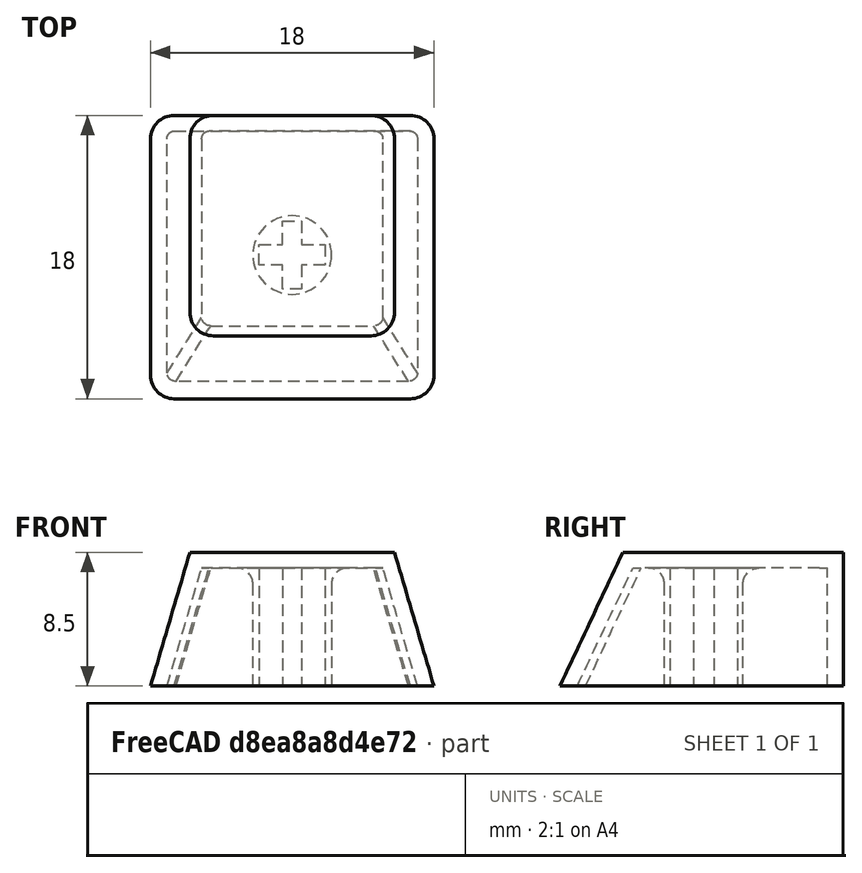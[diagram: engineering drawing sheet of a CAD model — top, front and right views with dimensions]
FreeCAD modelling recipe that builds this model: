
FCSTD DOCUMENT  (FreeCAD 0.20R29603 (Git))
Label: basecapv2
License: All rights reserved
LicenseURL: http://en.wikipedia.org/wiki/All_rights_reserved
objects: Sketcher::SketchObject×3, PartDesign::AdditiveLoft×1, PartDesign::Thickness×1, Mesh::Feature×1, PartDesign::Pad×1, PartDesign::Fillet×1, PartDesign::Body×1
note: 12 computed .brp shape members not serialized (recipe doc carries the construction recipe); baked Part::Feature solids carry a one-line shape summary decoded from their .brp

FEATURE [Sketcher::SketchObject] Sketch
  AttachmentOffset = pos=(0,0,8.5) rot=(0,0,1;0rad)
  FullyConstrained = true
  MapMode = 5
  Placement = pos=(0,0,8.5) rot=(0,0,1;0rad)
  Support = -> [XY_Plane]
  sketch-geometry (8):
    g0: LineSegment StartX=1.5 StartY=0 StartZ=0 EndX=11.5 EndY=0 EndZ=0
    g1: LineSegment StartX=13 StartY=1.5 StartZ=0 EndX=13 EndY=12.5 EndZ=0
    g2: LineSegment StartX=11.5 StartY=14 StartZ=0 EndX=1.5 EndY=14 EndZ=0
    g3: LineSegment StartX=2.849e-13 StartY=12.5 StartZ=0 EndX=2.849e-13 EndY=1.5 EndZ=0
    g4: ArcOfCircle CenterX=1.5 CenterY=12.5 CenterZ=0 NormalX=0 NormalY=0 NormalZ=1 AngleXU=0 Radius=1.5 StartAngle=1.5708 EndAngle=3.14159
    g5: ArcOfCircle CenterX=11.5 CenterY=12.5 CenterZ=0 NormalX=0 NormalY=0 NormalZ=1 AngleXU=0 Radius=1.5 StartAngle=-9e-16 EndAngle=1.5708
    g6: ArcOfCircle CenterX=11.5 CenterY=1.5 CenterZ=0 NormalX=0 NormalY=0 NormalZ=1 AngleXU=0 Radius=1.5 StartAngle=4.71239 EndAngle=6.28319
    g7: ArcOfCircle CenterX=1.5 CenterY=1.5 CenterZ=0 NormalX=0 NormalY=0 NormalZ=1 AngleXU=0 Radius=1.5 StartAngle=3.14159 EndAngle=4.71239
  constraints (20):
    c: Horizontal(g0)
    c: Horizontal(g2)
    c: Vertical(g1)
    c: Vertical(g3)
    c: Tangent(g3,g4) = -1.5708
    c: Tangent(g2,g4) = -1.5708
    c: Tangent(g1,g5) = -1.5708
    c: Tangent(g2,g5) = -1.5708
    c: Tangent(g0,g6) = -1.5708
    c: Tangent(g1,g6) = -1.5708
    c: Tangent(g3,g7) = -1.5708
    c: Tangent(g0,g7) = -1.5708
    c: Equal(g7,g4)
    c: Equal(g4,g5)
    c: Equal(g5,g6)
    c: Diameter(g5) = 3
    c: DistanceX(g3,g1) = 13
    c: PointOnObject(g3,g-2)
    c: PointOnObject(g0,g-1)
    c: DistanceY(g0,g2) = 14
FEATURE [Sketcher::SketchObject] Sketch001
  ExternalGeometry = -> [Sketch]
  FullyConstrained = true
  MapMode = 5
  Support = -> [XY_Plane]
  sketch-geometry (12):
    g0: ArcOfCircle CenterX=-1 CenterY=12.5 CenterZ=0 NormalX=0 NormalY=0 NormalZ=1 AngleXU=0 Radius=1.5 StartAngle=1.5708 EndAngle=3.14159
    g1: LineSegment StartX=-1 StartY=14 StartZ=0 EndX=14 EndY=14 EndZ=0
    g2: ArcOfCircle CenterX=14 CenterY=12.5 CenterZ=0 NormalX=0 NormalY=0 NormalZ=1 AngleXU=0 Radius=1.5 StartAngle=2e-16 EndAngle=1.5708
    g3: LineSegment StartX=15.5 StartY=12.5 StartZ=0 EndX=15.5 EndY=-2.5 EndZ=0
    g4: ArcOfCircle CenterX=14 CenterY=-2.5 CenterZ=0 NormalX=0 NormalY=0 NormalZ=1 AngleXU=0 Radius=1.5 StartAngle=4.71239 EndAngle=6.28319
    g5: LineSegment StartX=14 StartY=-4 StartZ=0 EndX=-1 EndY=-4 EndZ=0
    g6: ArcOfCircle CenterX=-1 CenterY=-2.5 CenterZ=0 NormalX=0 NormalY=0 NormalZ=1 AngleXU=0 Radius=1.5 StartAngle=3.14159 EndAngle=4.71239
    g7: LineSegment StartX=-2.5 StartY=-2.5 StartZ=0 EndX=-2.5 EndY=12.5 EndZ=0
    g8: GeomPoint X=-2.5 Y=14 Z=0
    g9: GeomPoint X=15.5 Y=-4 Z=0
    g10: LineSegment StartX=2.849e-13 StartY=12.5 StartZ=0 EndX=-2.5 EndY=12.5 EndZ=0
    g11: LineSegment StartX=13 StartY=12.5 StartZ=0 EndX=15.5 EndY=12.5 EndZ=0
  constraints (28):
    c: Tangent(g0,g1) = 1.5708
    c: Tangent(g1,g2) = 1.5708
    c: Tangent(g2,g3) = 1.5708
    c: Tangent(g3,g4) = 1.5708
    c: Tangent(g4,g5) = 1.5708
    c: Tangent(g5,g6) = 1.5708
    c: Tangent(g6,g7) = 1.5708
    c: Tangent(g7,g0) = 1.5708
    c: Horizontal(g1)
    c: Horizontal(g5)
    c: Vertical(g3)
    c: Vertical(g7)
    c: Equal(g0,g2)
    c: Equal(g2,g4)
    c: Equal(g4,g6)
    c: PointOnObject(g8,g1)
    c: PointOnObject(g8,g7)
    c: PointOnObject(g9,g3)
    c: PointOnObject(g9,g5)
    c: Diameter(g2) = 3
    c: DistanceX(g0,g2) = 18
    c: DistanceY(g4,g1) = 18
    c: PointOnObject(g-3,g1)
    c: Coincident(g10,g-4)
    c: Coincident(g10,g0)
    c: Coincident(g11,g-5)
    c: Coincident(g11,g2)
    c: Equal(g11,g10)
FEATURE [PartDesign::AdditiveLoft] AdditiveLoft
  Closed = false
  Profile = -> Sketch001
  Ruled = false
  Sections = -> [Sketch]
FEATURE [PartDesign::Thickness] Thickness
  Base = -> AdditiveLoft [Face1]
  BaseFeature = -> AdditiveLoft
  Intersection = false
  Join = 0
  Mode = 0
  Reversed = true
  SupportTransform = false
  Value = 1
FEATURE [Mesh::Feature] cherry_mx_key_cap
  Placement = pos=(17.8,14,0) rot=(0,0,1;4.71239rad)
FEATURE [Sketcher::SketchObject] Sketch002
  ExternalGeometry = -> [Thickness]
  FullyConstrained = true
  MapMode = 5
  Placement = pos=(0,0,7.5) rot=(1,0,0;3.14159rad)
  Support = -> [Thickness]
  sketch-geometry (23):
    g0: Circle CenterX=6.5 CenterY=-5.13461 CenterZ=0 NormalX=0 NormalY=0 NormalZ=1 AngleXU=0 Radius=2.5
    g1: LineSegment StartX=0.748238 StartY=-5.13461 StartZ=0 EndX=6.5 EndY=-5.13461 EndZ=0
    g2: LineSegment StartX=6.5 StartY=-5.13461 StartZ=0 EndX=12.2518 EndY=-5.13461 EndZ=0
    g3: LineSegment StartX=6.5 StartY=-0.634606 StartZ=0 EndX=6.5 EndY=-5.13461 EndZ=0
    g4: LineSegment StartX=6.5 StartY=-5.13461 StartZ=0 EndX=6.5 EndY=-13 EndZ=0
    g5: LineSegment StartX=4.4 StartY=-4.48461 StartZ=0 EndX=4.4 EndY=-5.78461 EndZ=0
    g6: LineSegment StartX=4.4 StartY=-5.78461 StartZ=0 EndX=5.9 EndY=-5.78461 EndZ=0
    g7: LineSegment StartX=5.9 StartY=-5.78461 StartZ=0 EndX=5.9 EndY=-7.28461 EndZ=0
    g8: LineSegment StartX=5.9 StartY=-7.28461 StartZ=0 EndX=7.1 EndY=-7.28461 EndZ=0
    g9: LineSegment StartX=7.1 StartY=-7.28461 StartZ=0 EndX=7.1 EndY=-5.78461 EndZ=0
    g10: LineSegment StartX=7.1 StartY=-5.78461 StartZ=0 EndX=8.6 EndY=-5.78461 EndZ=0
    g11: LineSegment StartX=8.6 StartY=-5.78461 StartZ=0 EndX=8.6 EndY=-4.48461 EndZ=0
    g12: LineSegment StartX=8.6 StartY=-4.48461 StartZ=0 EndX=7.1 EndY=-4.48461 EndZ=0
    g13: LineSegment StartX=7.1 StartY=-4.48461 StartZ=0 EndX=7.1 EndY=-2.98461 EndZ=0
    g14: LineSegment StartX=7.1 StartY=-2.98461 StartZ=0 EndX=5.9 EndY=-2.98461 EndZ=0
    g15: LineSegment StartX=5.9 StartY=-2.98461 StartZ=0 EndX=5.9 EndY=-4.48461 EndZ=0
    g16: LineSegment StartX=5.9 StartY=-4.48461 StartZ=0 EndX=4.4 EndY=-4.48461 EndZ=0
    g17: LineSegment StartX=5.9 StartY=-4.48461 StartZ=0 EndX=7.1 EndY=-4.48461 EndZ=0
    g18: LineSegment StartX=7.1 StartY=-4.48461 StartZ=0 EndX=7.1 EndY=-5.78461 EndZ=0
    g19: LineSegment StartX=7.1 StartY=-5.78461 StartZ=0 EndX=5.9 EndY=-5.78461 EndZ=0
    g20: LineSegment StartX=5.9 StartY=-5.78461 StartZ=0 EndX=5.9 EndY=-4.48461 EndZ=0
    g21: LineSegment StartX=5.9 StartY=-5.78461 StartZ=0 EndX=6.5 EndY=-5.13461 EndZ=0
    g22: LineSegment StartX=6.5 StartY=-5.13461 StartZ=0 EndX=7.1 EndY=-4.48461 EndZ=0
  constraints (62):
    c: Diameter(g0) = 5
    c: PointOnObject(g1,g-3)
    c: Coincident(g1,g0)
    c: Horizontal(g1)
    c: Coincident(g1,g2)
    c: PointOnObject(g2,g-4)
    c: Horizontal(g2)
    c: PointOnObject(g3,g-5)
    c: Coincident(g3,g0)
    c: Coincident(g3,g4)
    c: PointOnObject(g4,g-6)
    c: Vertical(g4)
    c: Vertical(g3)
    c: Equal(g1,g2)
    c: Vertical(g5)
    c: Coincident(g5,g6)
    c: Horizontal(g6)
    c: Coincident(g6,g7)
    c: Vertical(g7)
    c: Coincident(g7,g8)
    c: Horizontal(g8)
    c: Coincident(g8,g9)
    c: Vertical(g9)
    c: Coincident(g9,g10)
    c: Horizontal(g10)
    c: Coincident(g10,g11)
    c: Vertical(g11)
    c: Coincident(g11,g12)
    c: Horizontal(g12)
    c: Coincident(g12,g13)
    c: Vertical(g13)
    c: Coincident(g13,g14)
    c: Horizontal(g14)
    c: Coincident(g14,g15)
    c: Vertical(g15)
    c: Coincident(g15,g16)
    c: Coincident(g16,g5)
    c: Horizontal(g16)
    c: Equal(g12,g16)
    c: Equal(g16,g15)
    c: Equal(g15,g7)
    c: Coincident(g17,g18)
    c: Coincident(g18,g19)
    c: Coincident(g19,g20)
    c: Coincident(g20,g17)
    c: Horizontal(g17)
    c: Horizontal(g19)
    c: Vertical(g18)
    c: Vertical(g20)
    c: Coincident(g17,g15)
    c: Coincident(g18,g9)
    c: Coincident(g12,g17)
    c: Coincident(g19,g6)
    c: DistanceX(g16,g16) = 1.5
    c: Coincident(g6,g21)
    c: Coincident(g22,g12)
    c: Tangent(g21,g22) = -1.5708
    c: Coincident(g21,g0)
    c: Equal(g22,g21)
    c: DistanceY(g5,g5) = 1.3
    c: DistanceY(g3,g3) = 4.5
    c: DistanceX(g8,g8) = 1.2
FEATURE [PartDesign::Pad] Pad
  BaseFeature = -> Thickness
  Direction = (0,0,-1)
  Length = 7.5
  Length2 = 10
  Profile = -> Sketch002
  ReferenceAxis = -> Sketch002 [N_Axis]
  Type = 0
FEATURE [PartDesign::Fillet] Fillet
  Base = -> Pad [Edge49]
  BaseFeature = -> Pad
  Radius = 1
  SupportTransform = false
  UseAllEdges = false
FEATURE [PartDesign::Body] Body
  Group = -> [Sketch,Sketch001,AdditiveLoft,Thickness,Sketch002,Pad,Fillet]
  Origin = -> Origin
  Tip = -> Fillet
